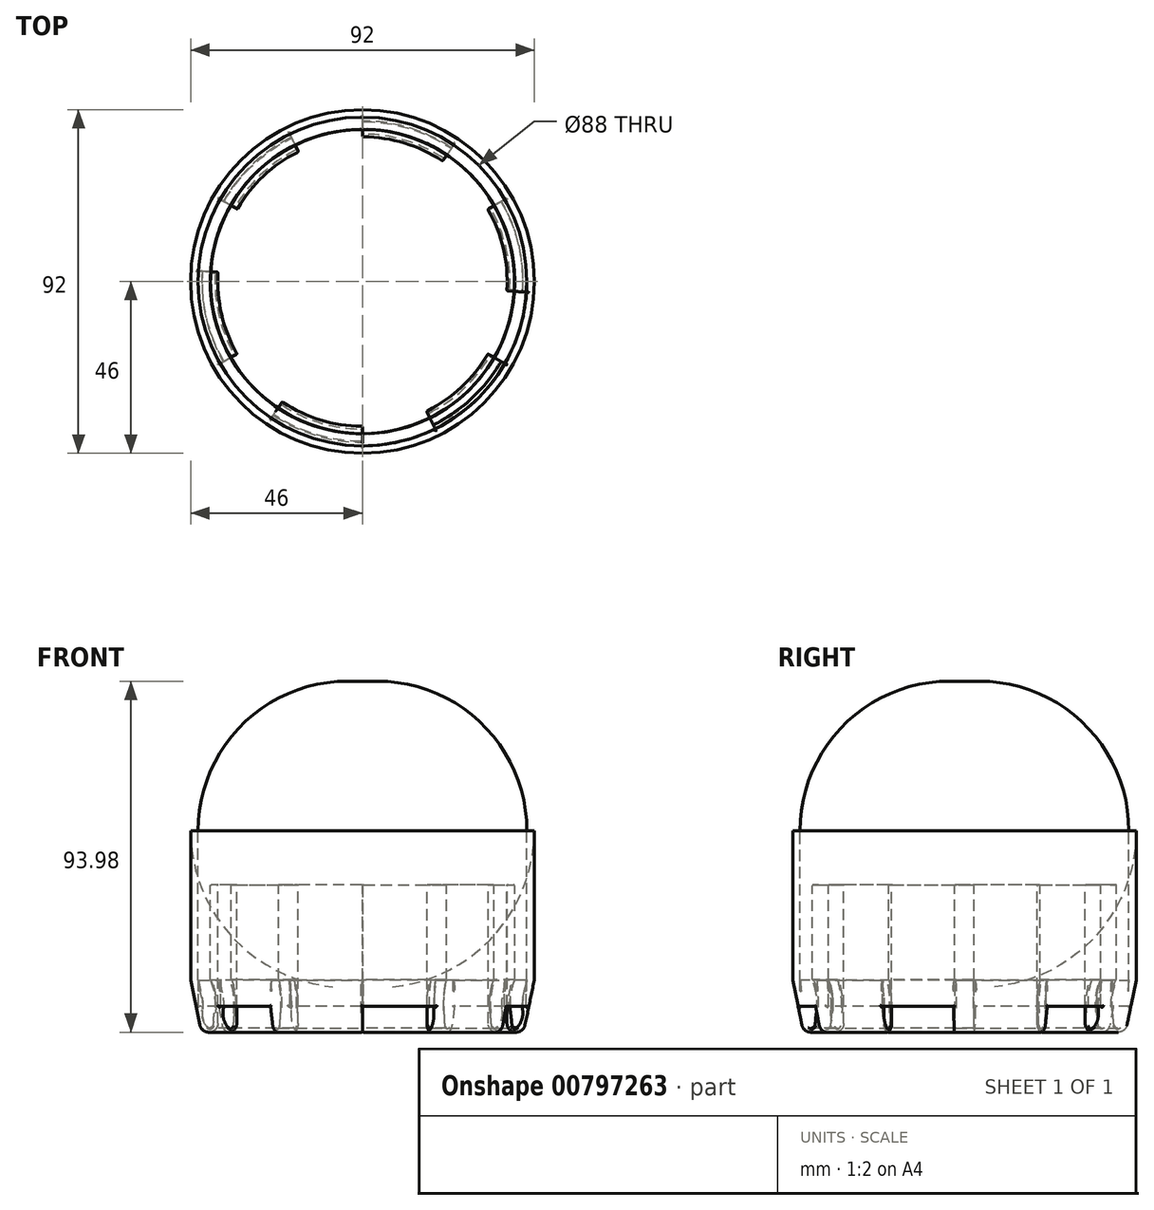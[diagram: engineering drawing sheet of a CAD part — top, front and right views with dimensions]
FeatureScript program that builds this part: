
annotation { "Feature Type Name" : "Feature", "Feature Type Description" : "" }
export const myFeature = defineFeature(function(context is Context, id is Id, definition is map)
    precondition{}
    {
        {
            var Q0;
            Q0=qCreatedBy(makeId("Front.planeOp"),FACE);
            var sketch = newSketch(context, id + "F0", { "sketchPlane" : qUnion([Q0])});
            skLineSegment(sketch, "E0", {"start": v(-44, -40) * mm, "end": v(-44, 0) * mm});
            skArc(sketch, "E1", {"start": v(-4, 40) * mm, "mid": v(-32.28, 28.28) * mm, "end": v(-44, 0) * mm});
            skLineSegment(sketch, "E2", {"start": v(-4, 40) * mm, "end": v(0, 40) * mm});
            skLineSegment(sketch, "E3", {"start": v(-44, -40) * mm, "end": v(-46, -40) * mm});
            skLineSegment(sketch, "E4", {"start": v(-46, -40) * mm, "end": v(-46, 0) * mm});
            skArc(sketch, "E5", {"start": v(0, 41.8) * mm, "mid": v(-32.25, 31.08) * mm, "end": v(-46, 0) * mm});
            skLineSegment(sketch, "E6", {"start": v(0, 41.8) * mm, "end": v(0, 40) * mm});
            skLineSegment(sketch, "E7", {"start": v(0, 0) * mm, "end": v(0, -40) * mm});
            skLineSegment(sketch, "E8", {"start": v(-46, -40) * mm, "end": v(-43.5, -52.06) * mm});
            skLineSegment(sketch, "E9", {"start": v(-40.74, -14.52) * mm, "end": v(-40.74, -39.94) * mm});
            skLineSegment(sketch, "E10", {"start": v(-40.74, -14.52) * mm, "end": v(-38.74, -14.52) * mm});
            skLineSegment(sketch, "E11", {"start": v(-38.74, -14.52) * mm, "end": v(-38.74, -51.57) * mm});
            skArc(sketch, "E12", {"start": v(-43.5, -52.06) * mm, "mid": v(-40.9, -53.97) * mm, "end": v(-38.74, -51.57) * mm});
            skArc(sketch, "E13", {"start": v(-39.65, -48.8) * mm, "mid": v(-39.6, -44.3) * mm, "end": v(-40.74, -39.94) * mm});
            skPoint(sketch, "E13.startSnap0", {"position": v(-40.9, -53.97) * mm});
            skLineSegment(sketch, "E14", {"start": v(-44, -40) * mm, "end": v(-43.01, -44.79) * mm});
            skArc(sketch, "E15", {"start": v(-42.94, -48.03) * mm, "mid": v(-42.83, -46.4) * mm, "end": v(-43.01, -44.79) * mm});
            skArc(sketch, "E16", {"start": v(-42.94, -48.03) * mm, "mid": v(-42.79, -50.43) * mm, "end": v(-41.61, -52.53) * mm});
            skArc(sketch, "E17", {"start": v(-41.61, -52.53) * mm, "mid": v(-40.74, -52.8) * mm, "end": v(-40.08, -52.18) * mm});
            skLineSegment(sketch, "E18", {"start": v(-40.74, -39.94) * mm, "end": v(-40.74, -39.94) * mm});
            skArc(sketch, "E19", {"start": v(-39.9, -51.11) * mm, "mid": v(-39.8, -49.95) * mm, "end": v(-39.65, -48.8) * mm});
            skArc(sketch, "E20", {"start": v(-39.9, -51.11) * mm, "mid": v(-39.96, -51.65) * mm, "end": v(-40.08, -52.18) * mm});
            skSolve(sketch);
        }
        {
            var Q0;
            Q0 = qSketchRegion(id + "F0", true);
            var Q1;
            Q1=sQuery(id+"F0.wireOp",EDGE,"E7");
            revolve(context, id + "F1", {"surfaceOperationType" : NewSurfaceOperationType.NEW, "entities" : qUnion([Q0]), "axis" : qUnion([Q1]), "revolveType" : RevolveType.FULL});
        }
        {
            var Q0;
            Q0=qCreatedBy(makeId("Top.planeOp"),FACE);
            var sketch = newSketch(context, id + "F2", { "sketchPlane" : qUnion([Q0])});
            skArc(sketch, "E21", {"start": v(0, 44) * mm, "mid": v(-10, 42.85) * mm, "end": v(-19.48, 39.45) * mm});
            skLineSegment(sketch, "E22", {"start": v(-19.48, 39.45) * mm, "end": v(-14.16, 28.7) * mm});
            skLineSegment(sketch, "E23", {"start": v(0, 44) * mm, "end": v(0, 32) * mm});
            skArc(sketch, "E24", {"start": v(0, 32) * mm, "mid": v(-7.27, 31.16) * mm, "end": v(-14.16, 28.7) * mm});
            skArc(sketch, "E25.1.0", {"start": v(-27.71, 16) * mm, "mid": v(-30.62, 9.28) * mm, "end": v(-31.93, 2.08) * mm});
            skLineSegment(sketch, "E25.1.1", {"start": v(-43.9, 2.86) * mm, "end": v(-31.93, 2.08) * mm});
            skArc(sketch, "E25.1.2", {"start": v(-38.1, 22) * mm, "mid": v(-42.1, 12.76) * mm, "end": v(-43.9, 2.86) * mm});
            skLineSegment(sketch, "E25.1.3", {"start": v(-38.1, 22) * mm, "end": v(-27.71, 16) * mm});
            skArc(sketch, "E25.2.0", {"start": v(-27.71, -16) * mm, "mid": v(-23.35, -21.88) * mm, "end": v(-17.77, -26.61) * mm});
            skLineSegment(sketch, "E25.2.1", {"start": v(-24.43, -36.6) * mm, "end": v(-17.77, -26.61) * mm});
            skArc(sketch, "E25.2.2", {"start": v(-38.1, -22) * mm, "mid": v(-32.1, -30.08) * mm, "end": v(-24.43, -36.6) * mm});
            skLineSegment(sketch, "E25.2.3", {"start": v(-38.1, -22) * mm, "end": v(-27.71, -16) * mm});
            skArc(sketch, "E26.3.3.0", {"start": v(0, -32) * mm, "mid": v(7.27, -31.16) * mm, "end": v(14.16, -28.7) * mm});
            skLineSegment(sketch, "E26.4.3.0", {"start": v(19.48, -39.45) * mm, "end": v(14.16, -28.7) * mm});
            skArc(sketch, "E26.7.3.0", {"start": v(0, -44) * mm, "mid": v(10, -42.85) * mm, "end": v(19.48, -39.45) * mm});
            skLineSegment(sketch, "E26.11.3.0", {"start": v(0, -44) * mm, "end": v(0, -32) * mm});
            skArc(sketch, "E26.3.4.0", {"start": v(27.71, -16) * mm, "mid": v(30.62, -9.28) * mm, "end": v(31.93, -2.08) * mm});
            skLineSegment(sketch, "E26.4.4.0", {"start": v(43.9, -2.86) * mm, "end": v(31.93, -2.08) * mm});
            skArc(sketch, "E26.7.4.0", {"start": v(38.1, -22) * mm, "mid": v(42.1, -12.76) * mm, "end": v(43.9, -2.86) * mm});
            skLineSegment(sketch, "E26.11.4.0", {"start": v(38.1, -22) * mm, "end": v(27.71, -16) * mm});
            skArc(sketch, "E26.3.5.0", {"start": v(27.71, 16) * mm, "mid": v(23.35, 21.88) * mm, "end": v(17.77, 26.61) * mm});
            skLineSegment(sketch, "E26.4.5.0", {"start": v(24.43, 36.6) * mm, "end": v(17.77, 26.61) * mm});
            skArc(sketch, "E26.7.5.0", {"start": v(38.1, 22) * mm, "mid": v(32.1, 30.08) * mm, "end": v(24.43, 36.6) * mm});
            skLineSegment(sketch, "E26.11.5.0", {"start": v(38.1, 22) * mm, "end": v(27.71, 16) * mm});
            skSolve(sketch);
        }
        {
            var Q0;
            Q0 = qSketchRegion(id + "F2", true);
            extrude(context, id + "F3", {"entities" : qUnion([Q0]), "operationType" : NewBodyOperationType.REMOVE, "endBound" : BoundingType.THROUGH_ALL, "oppositeDirection" : true, "depth" : 25 * mm, "offsetDistance" : 25 * mm});
        }
        {
            var Q0;
            Q0=makeQuery(id+"F1.opRevolve","SWEPT_FACE",FACE,{"disambiguationData":[OSD([sQuery(id+"F0.wireOp",EDGE,"E8")])]});
            fillet(context, id + "F4", {"entities" : qUnion([Q0]), "radius" : 0.3 * mm, "tangentPropagation" : true, "allowEdgeOverflow" : false});
        }
        {
            var Q0;
            Q0=makeQuery(id+"F3.boolean.opBoolean","COPY",FACE,{"derivedFrom":makeQuery(id+"F3.opExtrude","SWEPT_FACE",FACE,{"disambiguationData":[OSD([sQuery(id+"F2.wireOp",EDGE,"E25.1.1")])]})});
            fillet(context, id + "F5", {"entities" : qUnion([Q0]), "radius" : 0.3 * mm, "tangentPropagation" : true, "allowEdgeOverflow" : false});
        }
        {
            var Q0;
            Q0=makeQuery(id+"F3.boolean.opBoolean","COPY",FACE,{"derivedFrom":makeQuery(id+"F3.opExtrude","SWEPT_FACE",FACE,{"disambiguationData":[OSD([sQuery(id+"F2.wireOp",EDGE,"E22")])]})});
            fillet(context, id + "F6", {"entities" : qUnion([Q0]), "radius" : 0.3 * mm, "tangentPropagation" : true, "allowEdgeOverflow" : false});
        }
        {
            var Q0;
            Q0=makeQuery(id+"F3.boolean.opBoolean","COPY",FACE,{"derivedFrom":makeQuery(id+"F3.opExtrude","SWEPT_FACE",FACE,{"disambiguationData":[OSD([sQuery(id+"F2.wireOp",EDGE,"E26.4.5.0")])]})});
            fillet(context, id + "F7", {"entities" : qUnion([Q0]), "radius" : 0.3 * mm, "tangentPropagation" : true, "allowEdgeOverflow" : false});
        }
        {
            var Q0;
            Q0=makeQuery(id+"F3.boolean.opBoolean","COPY",FACE,{"derivedFrom":makeQuery(id+"F3.opExtrude","SWEPT_FACE",FACE,{"disambiguationData":[OSD([sQuery(id+"F2.wireOp",EDGE,"E26.4.4.0")])]})});
            fillet(context, id + "F8", {"entities" : qUnion([Q0]), "radius" : 0.3 * mm, "tangentPropagation" : true, "allowEdgeOverflow" : false});
        }
        {
            var Q0;
            Q0=makeQuery(id+"F3.boolean.opBoolean","COPY",FACE,{"derivedFrom":makeQuery(id+"F3.opExtrude","SWEPT_FACE",FACE,{"disambiguationData":[OSD([sQuery(id+"F2.wireOp",EDGE,"E26.4.3.0")])]})});
            fillet(context, id + "F9", {"entities" : qUnion([Q0]), "radius" : 0.3 * mm, "tangentPropagation" : true, "allowEdgeOverflow" : false});
        }
        {
            var Q0;
            Q0=makeQuery(id+"F3.boolean.opBoolean","COPY",FACE,{"derivedFrom":makeQuery(id+"F3.opExtrude","SWEPT_FACE",FACE,{"disambiguationData":[OSD([sQuery(id+"F2.wireOp",EDGE,"E25.2.1")])]})});
            fillet(context, id + "F10", {"entities" : qUnion([Q0]), "radius" : 0.3 * mm, "tangentPropagation" : true, "allowEdgeOverflow" : false});
        }
        {
            var Q0;
            Q0=makeQuery(id+"F3.boolean.opBoolean","COPY",FACE,{"derivedFrom":makeQuery(id+"F3.opExtrude","SWEPT_FACE",FACE,{"disambiguationData":[OSD([sQuery(id+"F2.wireOp",EDGE,"E25.2.3")])]})});
            fillet(context, id + "F11", {"entities" : qUnion([Q0]), "radius" : 0.3 * mm, "tangentPropagation" : true, "allowEdgeOverflow" : false});
        }
        {
            var Q0;
            Q0=makeQuery(id+"F3.boolean.opBoolean","COPY",FACE,{"derivedFrom":makeQuery(id+"F3.opExtrude","SWEPT_FACE",FACE,{"disambiguationData":[OSD([sQuery(id+"F2.wireOp",EDGE,"E25.1.3")])]})});
            fillet(context, id + "F12", {"entities" : qUnion([Q0]), "radius" : 0.3 * mm, "tangentPropagation" : true, "allowEdgeOverflow" : false});
        }
        {
            var Q0;
            Q0=makeQuery(id+"F3.boolean.opBoolean","COPY",FACE,{"derivedFrom":makeQuery(id+"F3.opExtrude","SWEPT_FACE",FACE,{"disambiguationData":[OSD([sQuery(id+"F2.wireOp",EDGE,"E23")])]})});
            fillet(context, id + "F13", {"entities" : qUnion([Q0]), "radius" : 0.3 * mm, "tangentPropagation" : true, "allowEdgeOverflow" : false});
        }
        {
            var Q0;
            Q0=makeQuery(id+"F3.boolean.opBoolean","COPY",FACE,{"derivedFrom":makeQuery(id+"F3.opExtrude","SWEPT_FACE",FACE,{"disambiguationData":[OSD([sQuery(id+"F2.wireOp",EDGE,"E26.11.5.0")])]})});
            fillet(context, id + "F14", {"entities" : qUnion([Q0]), "radius" : 0.3 * mm, "tangentPropagation" : true, "allowEdgeOverflow" : false});
        }
        {
            var Q0;
            Q0=makeQuery(id+"F3.boolean.opBoolean","COPY",FACE,{"derivedFrom":makeQuery(id+"F3.opExtrude","SWEPT_FACE",FACE,{"disambiguationData":[OSD([sQuery(id+"F2.wireOp",EDGE,"E26.11.4.0")])]})});
            fillet(context, id + "F15", {"entities" : qUnion([Q0]), "radius" : 0.3 * mm, "tangentPropagation" : true, "allowEdgeOverflow" : false});
        }
        {
            var Q0;
            Q0=makeQuery(id+"F3.boolean.opBoolean","COPY",FACE,{"derivedFrom":makeQuery(id+"F3.opExtrude","SWEPT_FACE",FACE,{"disambiguationData":[OSD([sQuery(id+"F2.wireOp",EDGE,"E26.11.3.0")])]})});
            fillet(context, id + "F16", {"entities" : qUnion([Q0]), "radius" : 0.3 * mm, "tangentPropagation" : true, "allowEdgeOverflow" : false});
        }
    });
